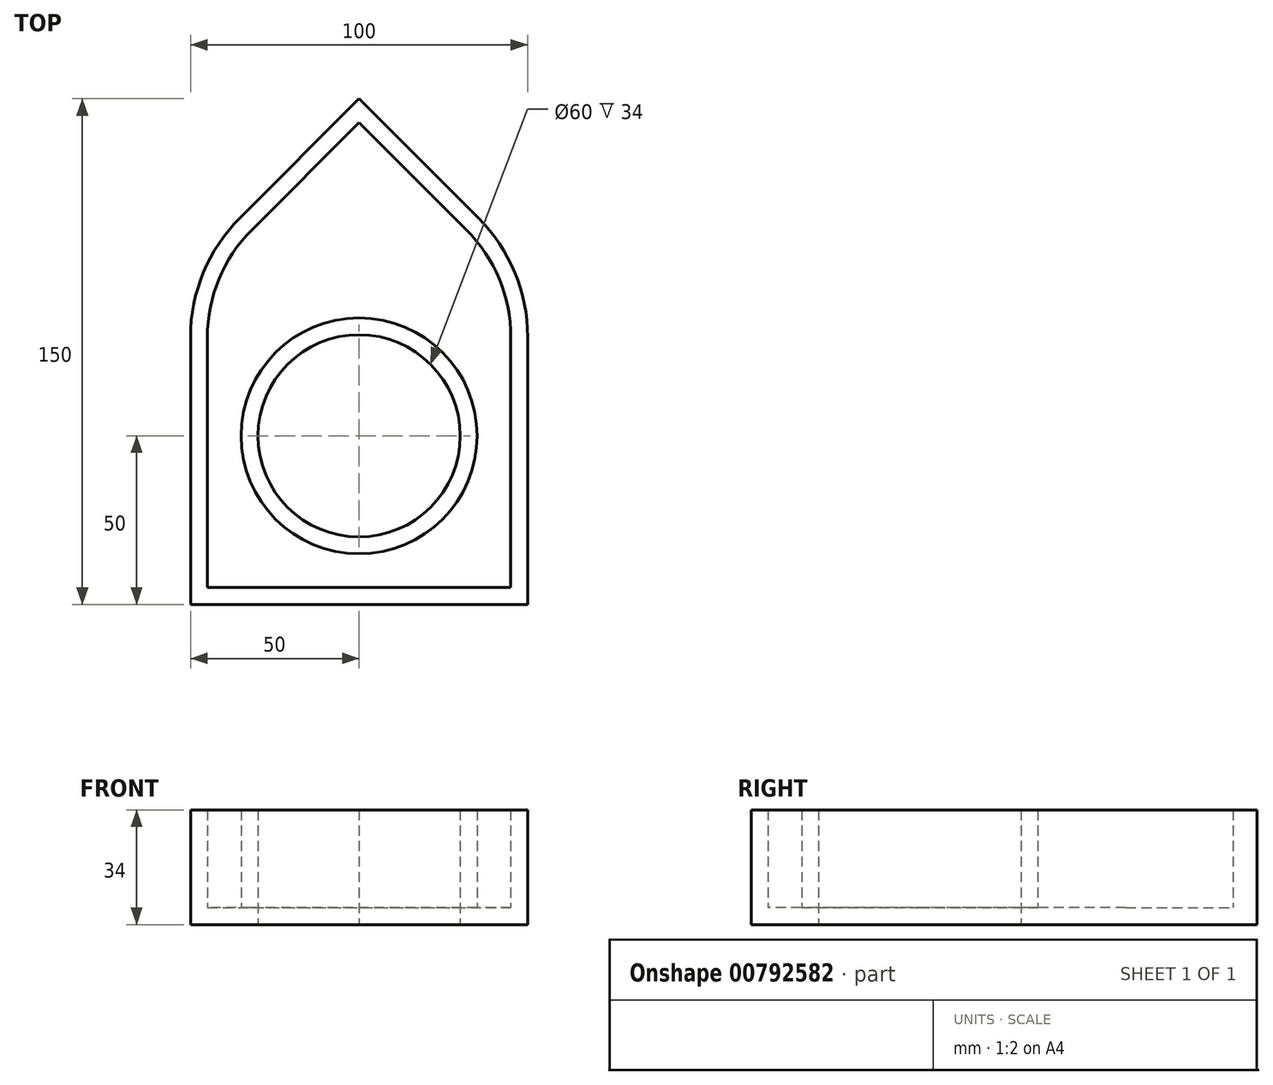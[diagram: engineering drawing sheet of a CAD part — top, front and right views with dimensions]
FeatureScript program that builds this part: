
annotation { "Feature Type Name" : "Feature", "Feature Type Description" : "" }
export const myFeature = defineFeature(function(context is Context, id is Id, definition is map)
    precondition{}
    {
        {
            var Q0;
            Q0=qCreatedBy(makeId("Top.planeOp"),FACE);
            var sketch = newSketch(context, id + "F0", { "sketchPlane" : qUnion([Q0])});
            skLineSegment(sketch, "E0.bottom", {"start": v(-50, 50) * mm, "end": v(50, 50) * mm});
            skLineSegment(sketch, "E0.top", {"start": v(-50, -50) * mm, "end": v(50, -50) * mm});
            skLineSegment(sketch, "E0.left", {"start": v(-50, 50) * mm, "end": v(-50, -50) * mm});
            skLineSegment(sketch, "E0.right", {"start": v(50, 50) * mm, "end": v(50, -50) * mm});
            skCircle(sketch, "E1", {"center": v(0, 0) * mm, "radius": 30 * mm});
            skLineSegment(sketch, "E2", {"start": v(-50, 50) * mm, "end": v(0, 100) * mm});
            skLineSegment(sketch, "E3", {"start": v(0, 100) * mm, "end": v(50, 50) * mm});
            skLineSegment(sketch, "E4", {"start": v(-50, 50) * mm, "end": v(50, -50) * mm, "construction": true});
            skSolve(sketch);
        }
        {
            var Q0;
            Q0=makeQuery(id+"F0.imprint","IMPRINT",FACE,{"disambiguationData":[TD([[makeQuery(id+"F0.imprint","IMPRINT",EDGE,{"derivedFrom":sQuery(id+"F0.wireOp",EDGE,"E0.bottom")}),1.0]])]});
            var Q1;
            Q1=makeQuery(id+"F0.imprint","IMPRINT",FACE,{"disambiguationData":[TD([[makeQuery(id+"F0.imprint","IMPRINT",EDGE,{"derivedFrom":sQuery(id+"F0.wireOp",EDGE,"E0.bottom")}),-1.0]])]});
            extrude(context, id + "F1", {"entities" : qUnion([Q0, Q1]), "depth" : 34 * mm, "offsetDistance" : 25 * mm});
        }
        {
            var Q0;
            Q0=makeQuery(id+"F1.opExtrude","SWEPT_EDGE",EDGE,{"disambiguationData":[OSD([sQuery(id+"F0.wireOp",EDGE,"E0.bottom"),sQuery(id+"F0.wireOp",EDGE,"E0.left"),sQuery(id+"F0.wireOp",EDGE,"E2")])]});
            var Q1;
            Q1=makeQuery(id+"F1.opExtrude","SWEPT_EDGE",EDGE,{"disambiguationData":[OSD([sQuery(id+"F0.wireOp",EDGE,"E0.bottom"),sQuery(id+"F0.wireOp",EDGE,"E0.right"),sQuery(id+"F0.wireOp",EDGE,"E3")])]});
            fillet(context, id + "F2", {"entities" : qUnion([Q0, Q1]), "radius" : 50 * mm, "tangentPropagation" : true, "allowEdgeOverflow" : false});
        }
        {
            var Q0;
            Q0=makeQuery(id+"F1.opExtrude","CAP_FACE",FACE,{"disambiguationData":[OSD([sQuery(id+"F0.wireOp",EDGE,"E0.top"),sQuery(id+"F0.wireOp",EDGE,"E0.left"),sQuery(id+"F0.wireOp",EDGE,"E0.right"),sQuery(id+"F0.wireOp",EDGE,"E1"),sQuery(id+"F0.wireOp",EDGE,"E2"),sQuery(id+"F0.wireOp",EDGE,"E3")])],"isStart":false});
            shell(context, id + "F3", {"entities" : qUnion([Q0]), "thickness" : 5 * mm});
        }
    });
